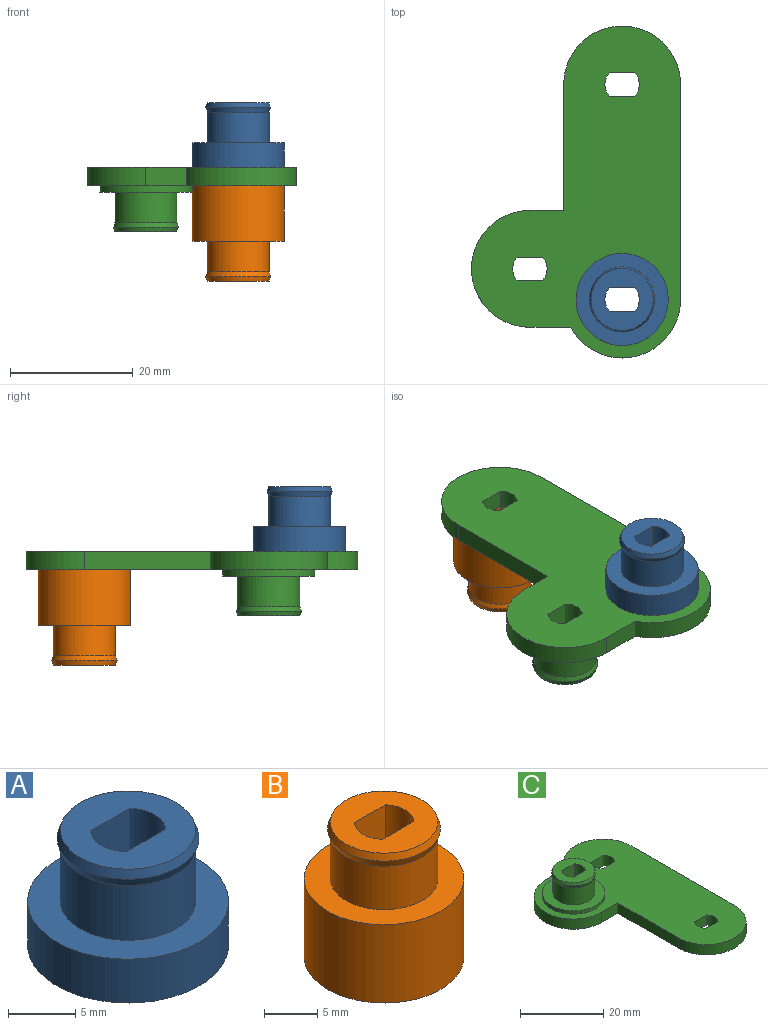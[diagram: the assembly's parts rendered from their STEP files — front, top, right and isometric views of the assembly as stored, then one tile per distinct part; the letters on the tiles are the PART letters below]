
ASSEMBLY  parts=3 mates=2
PART A: 11 faces, bbox 15x15x10.5 mm
  f0: plane 15x15mm, normal (0,0,1), area 96.6mm2, adj f4,f7
  f1: cylinder r=2.8mm len=10.5mm, axis (0,0,-1), area 43.9mm2, adj f2,f5,f6,f8
  f2: plane 10.5x4.11mm, normal (0,-1,0), area 43.2mm2, adj f1,f3,f6,f8
  f3: cylinder r=2.8mm len=10.5mm, axis (0,0,-1), area 43.9mm2, adj f2,f5,f6,f8
  f4: cylinder r=7.5mm len=15mm, axis (0,0,-1), area 188.5mm2, adj f0,f6
  f5: plane 10.5x4.11mm, normal (0,1,0), area 43.2mm2, adj f1,f3,f6,f8
  f6: plane 15x15mm, normal (0,0,-1), area 157.2mm2, adj f1,f2,f3,f4,f5
  f7: cylinder r=5.05mm len=10.1mm, axis (0,0,-1), area 158.7mm2, adj f0,f9
  f8: plane 10.1x10.1mm, normal (0,0,1), area 60.6mm2, adj f1,f2,f3,f5,f10
  f9: cone r=5.3mm half-angle=18.4deg, axis (0,0,1), area 25.7mm2, adj f7,f10
  f10: cone r=5.05mm half-angle=18.4deg, axis (0,0,-1), area 25.7mm2, adj f8,f9
PART B: 11 faces, bbox 15x15x15.5 mm
  f0: plane 15x15mm, normal (0,0,1), area 96.6mm2, adj f4,f7
  f1: cylinder r=2.8mm len=15.5mm, axis (0,0,-1), area 64.7mm2, adj f2,f5,f6,f8
  f2: plane 15.5x4.11mm, normal (0,-1,0), area 63.8mm2, adj f1,f3,f6,f8
  f3: cylinder r=2.8mm len=15.5mm, axis (0,0,-1), area 64.7mm2, adj f2,f5,f6,f8
  f4: cylinder r=7.5mm len=15mm, axis (0,0,-1), area 424.1mm2, adj f0,f6
  f5: plane 15.5x4.11mm, normal (0,1,0), area 63.8mm2, adj f1,f3,f6,f8
  f6: plane 15x15mm, normal (0,0,-1), area 157.2mm2, adj f1,f2,f3,f4,f5
  f7: cylinder r=5.05mm len=10.1mm, axis (0,0,-1), area 158.7mm2, adj f0,f9
  f8: plane 10.1x10.1mm, normal (0,0,1), area 60.6mm2, adj f1,f2,f3,f5,f10
  f9: cone r=5.3mm half-angle=18.4deg, axis (0,0,1), area 25.7mm2, adj f7,f10
  f10: cone r=5.05mm half-angle=18.4deg, axis (0,0,-1), area 25.7mm2, adj f8,f9
PART C: 27 faces, bbox 34x54x10.5 mm
  f0: cylinder r=9.5mm len=19mm, axis (0,0,-1), area 89.5mm2, adj f1,f6,f7,f8
  f1: plane 35x3mm, normal (1,0,0), area 105mm2, adj f0,f2,f7,f8
  f2: cylinder r=9.5mm len=17.87mm, axis (0,0,-1), area 75.5mm2, adj f1,f3,f7,f8
  f3: plane 6.63x3mm, normal (0,1,0), area 19.9mm2, adj f2,f4,f7,f8
  f4: cylinder r=9.5mm len=19mm, axis (0,0,-1), area 89.5mm2, adj f3,f5,f7,f8
  f5: plane 5.5x3mm, normal (0,-1,0), area 16.5mm2, adj f4,f6,f7,f8
  f6: plane 20.5x3mm, normal (-1,0,0), area 61.5mm2, adj f0,f5,f7,f8
  f7: plane 54x34mm, normal (0,0,1), area 980.7mm2, adj f0,f1,f2,f3,f4,f5,f6,f14
  f8: plane 54x34mm, normal (0,0,-1), area 1137.9mm2, adj f0,f1,f2,f3,f4,f5,f6,f10
  f9: cylinder r=5.05mm len=10.1mm, axis (0,0,-1), area 158.7mm2, adj f15,f17
  f10: cylinder r=2.8mm len=10.5mm, axis (0,0,-1), area 43.9mm2, adj f8,f11,f13,f16
  f11: plane 10.5x4.11mm, normal (0,-1,0), area 43.2mm2, adj f8,f10,f12,f16
  f12: cylinder r=2.8mm len=10.5mm, axis (0,0,-1), area 43.9mm2, adj f8,f11,f13,f16
  f13: plane 10.5x4.11mm, normal (0,1,0), area 43.2mm2, adj f8,f10,f12,f16
  f14: cylinder r=7.5mm len=15mm, axis (0,0,-1), area 47.1mm2, adj f7,f15
  f15: plane 15x15mm, normal (0,0,1), area 96.6mm2, adj f9,f14
  f16: plane 10.1x10.1mm, normal (0,0,1), area 60.6mm2, adj f10,f11,f12,f13,f18
  f17: cone r=5.3mm half-angle=18.4deg, axis (0,0,1), area 25.7mm2, adj f9,f18
  f18: cone r=5.05mm half-angle=18.4deg, axis (0,0,-1), area 25.7mm2, adj f16,f17
  f19: plane 4.11x3mm, normal (0,-1,0), area 12.3mm2, adj f7,f8,f20,f22
  f20: cylinder r=2.8mm len=3.8mm, axis (0,0,-1), area 12.5mm2, adj f7,f8,f19,f21
  f21: plane 4.11x3mm, normal (0,1,0), area 12.3mm2, adj f7,f8,f20,f22
  f22: cylinder r=2.8mm len=3.8mm, axis (0,0,-1), area 12.5mm2, adj f7,f8,f19,f21
  f23: plane 4.11x3mm, normal (0,-1,0), area 12.3mm2, adj f7,f8,f24,f26
  f24: cylinder r=2.8mm len=3.8mm, axis (0,0,-1), area 12.5mm2, adj f7,f8,f23,f25
  f25: plane 4.11x3mm, normal (0,1,0), area 12.3mm2, adj f7,f8,f24,f26
  f26: cylinder r=2.8mm len=3.8mm, axis (0,0,-1), area 12.5mm2, adj f7,f8,f23,f25
PLACE A t=(30.45,23.16,5.62)mm
PLACE B rot(axis=(1,0,0),180deg) t=(30.45,58.16,2.62)mm
PLACE C rot(axis=(1,0,0),180deg) t=(10.45,43.16,5.62)mm
MATE fastened A.f4 <-> C.f2  axis (0,0,-1) through (30.45,23.16,5.62)mm
MATE fastened B.f4 <-> C.f0  axis (0,0,1) through (30.45,58.16,2.62)mm
